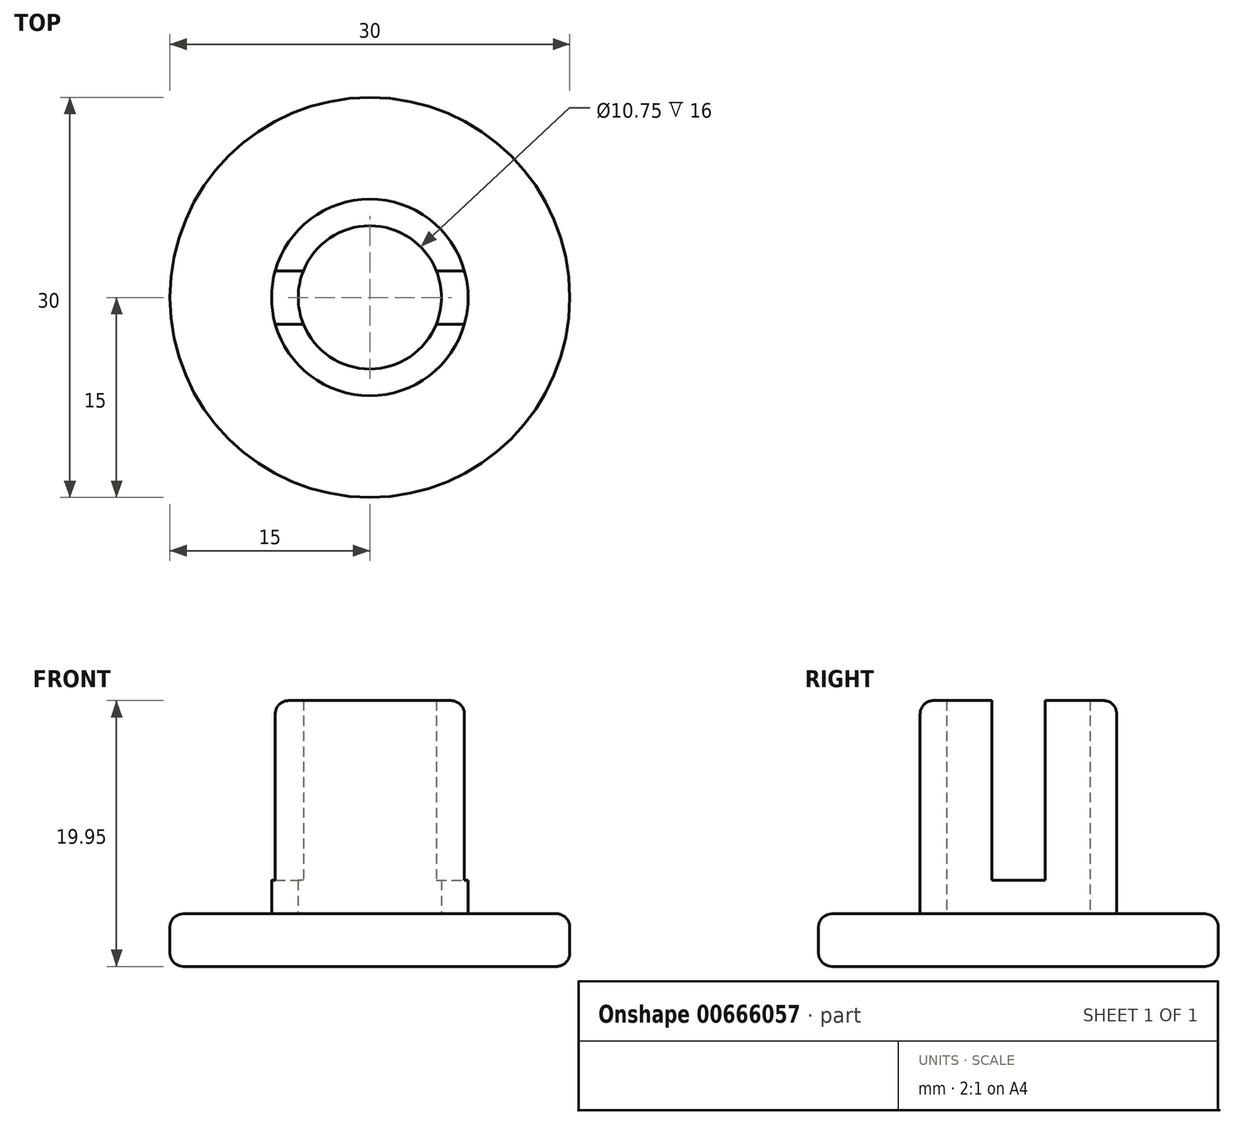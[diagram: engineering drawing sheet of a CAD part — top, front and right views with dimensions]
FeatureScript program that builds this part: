
annotation { "Feature Type Name" : "Feature", "Feature Type Description" : "" }
export const myFeature = defineFeature(function(context is Context, id is Id, definition is map)
    precondition{}
    {
        {
            var Q0;
            Q0=qCreatedBy(makeId("Top.planeOp"),FACE);
            var sketch = newSketch(context, id + "F0", { "sketchPlane" : qUnion([Q0])});
            skCircle(sketch, "E0", {"center": v(0, 0) * mm, "radius": 15 * mm});
            skSolve(sketch);
        }
        {
            var Q0;
            Q0 = qSketchRegion(id + "F0", true);
            extrude(context, id + "F1", {"entities" : qUnion([Q0]), "depth" : 3.95 * mm, "offsetDistance" : 25 * mm});
        }
        {
            var Q0;
            Q0=makeQuery(id+"F1.opExtrude","CAP_FACE",FACE,{"disambiguationData":[OSD([sQuery(id+"F0.wireOp",EDGE,"E0")])],"isStart":false});
            var sketch = newSketch(context, id + "F2", { "sketchPlane" : qUnion([Q0])});
            skCircle(sketch, "E1", {"center": v(0, 0) * mm, "radius": 7.38 * mm});
            skCircle(sketch, "E2.0", {"center": v(0, 0) * mm, "radius": 5.38 * mm});
            skSolve(sketch);
        }
        {
            var Q0;
            Q0 = qSketchRegion(id + "F2", true);
            extrude(context, id + "F3", {"entities" : qUnion([Q0]), "operationType" : NewBodyOperationType.ADD, "depth" : 16 * mm, "offsetDistance" : 25 * mm});
        }
        {
            var Q0;
            Q0=makeQuery(id+"F3.opExtrude","CAP_FACE",FACE,{"disambiguationData":[OSD([sQuery(id+"F2.wireOp",EDGE,"E1"),sQuery(id+"F2.wireOp",EDGE,"E2.0")])],"isStart":false});
            var sketch = newSketch(context, id + "F4", { "sketchPlane" : qUnion([Q0])});
            skLineSegment(sketch, "E3.bottom", {"start": v(11.68, 2) * mm, "end": v(-11.68, 2) * mm});
            skLineSegment(sketch, "E3.top", {"start": v(11.68, -2) * mm, "end": v(-11.68, -2) * mm});
            skLineSegment(sketch, "E3.left", {"start": v(11.68, 2) * mm, "end": v(11.68, -2) * mm});
            skLineSegment(sketch, "E3.right", {"start": v(-11.68, 2) * mm, "end": v(-11.68, -2) * mm});
            skPoint(sketch, "E3.middle", {"position": v(0, 0) * mm});
            skSolve(sketch);
        }
        {
            var Q0;
            Q0 = qSketchRegion(id + "F4", true);
            var Q1;
            {var subQ0=sQuery(id+"F0.wireOp",EDGE,"E0");Q1=makeQuery(id+"F3.boolean.opBoolean","SPLIT",FACE,{"disambiguationData":[TD([makeQuery(id+"F1.opExtrude","SWEPT_FACE",FACE,{"disambiguationData":[OSD([subQ0])]})])],"derivedFrom":makeQuery(id+"F1.opExtrude","CAP_FACE",FACE,{"disambiguationData":[OSD([subQ0])],"isStart":false})});}
            extrude(context, id + "F5", {"entities" : qUnion([Q0]), "operationType" : NewBodyOperationType.REMOVE, "endBound" : BoundingType.UP_TO_SURFACE, "oppositeDirection" : true, "depth" : 25 * mm, "endBoundEntityFace" : qUnion([Q1]), "hasOffset" : true, "offsetDistance" : 2.5 * mm});
        }
        {
            var Q0;
            {var subQ0=sQuery(id+"F2.wireOp",EDGE,"E1");Q0=makeQuery(id+"F5.boolean.opBoolean","SPLIT",EDGE,{"disambiguationData":[TD([makeQuery(id+"F5.opExtrude","SWEPT_FACE",FACE,{"disambiguationData":[OSD([sQuery(id+"F4.wireOp",EDGE,"E3.top")])]})])],"derivedFrom":makeQuery(id+"F3.opExtrude","CAP_EDGE",EDGE,{"disambiguationData":[OSD([subQ0])],"isStart":false})});}
            var Q1;
            {var subQ0=sQuery(id+"F2.wireOp",EDGE,"E1");Q1=makeQuery(id+"F5.boolean.opBoolean","SPLIT",EDGE,{"disambiguationData":[TD([makeQuery(id+"F5.opExtrude","SWEPT_FACE",FACE,{"disambiguationData":[OSD([sQuery(id+"F4.wireOp",EDGE,"E3.bottom")])]})])],"derivedFrom":makeQuery(id+"F3.opExtrude","CAP_EDGE",EDGE,{"disambiguationData":[OSD([subQ0])],"isStart":false})});}
            var Q2;
            Q2=makeQuery(id+"F1.opExtrude","SWEPT_FACE",FACE,{"disambiguationData":[OSD([sQuery(id+"F0.wireOp",EDGE,"E0")])]});
            fillet(context, id + "F6", {"entities" : qUnion([Q0, Q1, Q2]), "radius" : 1 * mm, "tangentPropagation" : true, "allowEdgeOverflow" : false});
        }
    });
